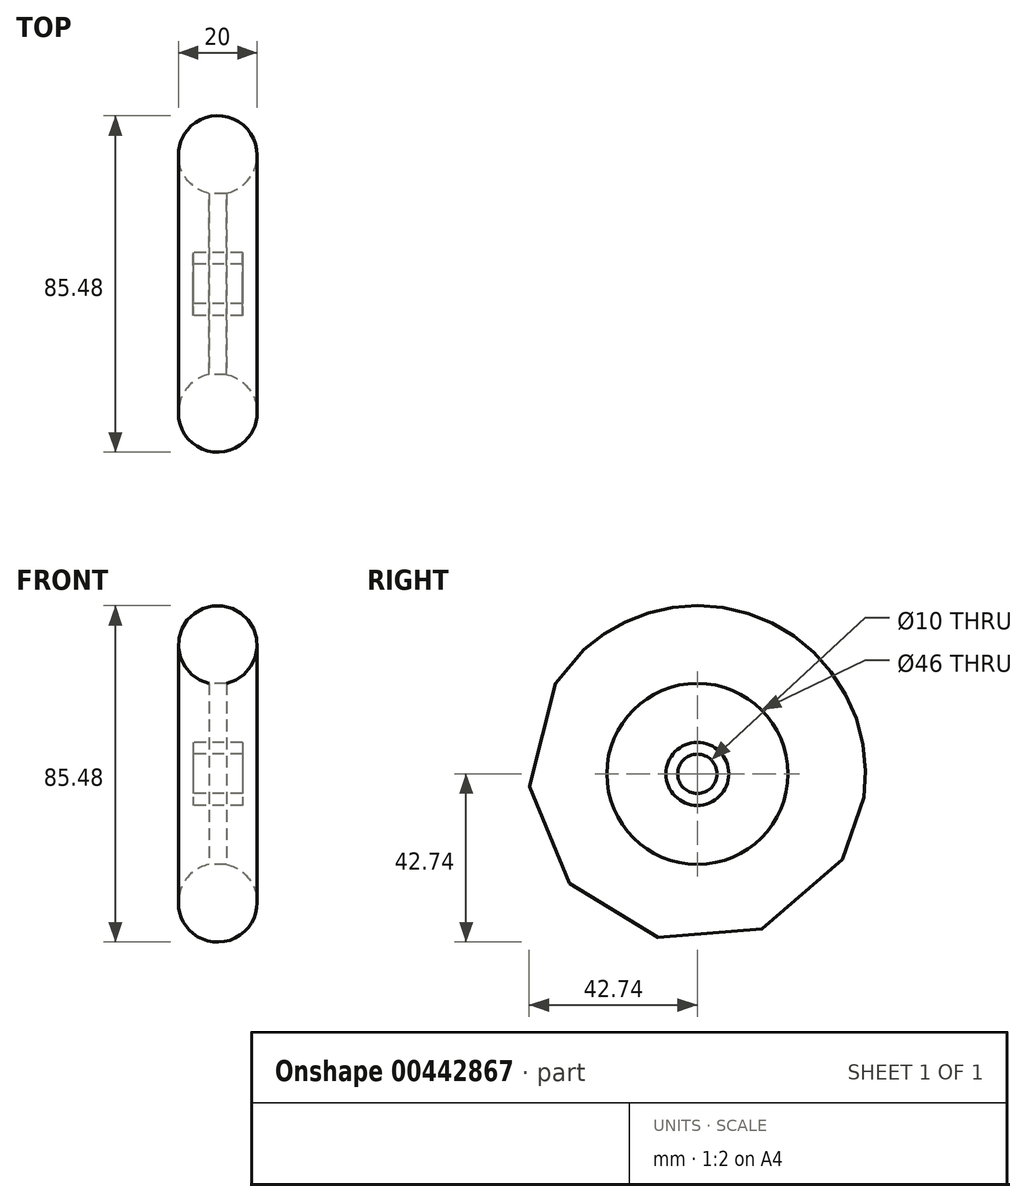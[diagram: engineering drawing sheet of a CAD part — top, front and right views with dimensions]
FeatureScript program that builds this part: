
annotation { "Feature Type Name" : "Feature", "Feature Type Description" : "" }
export const myFeature = defineFeature(function(context is Context, id is Id, definition is map)
    precondition{}
    {
        {
            var Q0;
            Q0=qCreatedBy(makeId("Front.planeOp"),FACE);
            var sketch = newSketch(context, id + "F0", { "sketchPlane" : qUnion([Q0])});
            skLineSegment(sketch, "E0.bottom", {"start": v(6.25, 8) * mm, "end": v(-6.25, 8) * mm});
            skLineSegment(sketch, "E0.top", {"start": v(6.25, 5) * mm, "end": v(-6.25, 5) * mm});
            skLineSegment(sketch, "E0.left", {"start": v(6.25, 8) * mm, "end": v(6.25, 5) * mm});
            skLineSegment(sketch, "E0.right", {"start": v(-6.25, 8) * mm, "end": v(-6.25, 5) * mm});
            skPoint(sketch, "E0.middle", {"position": v(0, 6.5) * mm});
            skLineSegment(sketch, "E1.bottom", {"start": v(-2.25, 8) * mm, "end": v(2.25, 8) * mm});
            skLineSegment(sketch, "E1.top", {"start": v(-2.25, 23) * mm, "end": v(2.25, 23) * mm});
            skLineSegment(sketch, "E1.left", {"start": v(-2.25, 8) * mm, "end": v(-2.25, 23) * mm});
            skLineSegment(sketch, "E1.right", {"start": v(2.25, 8) * mm, "end": v(2.25, 23) * mm});
            skArc(sketch, "E2", {"start": v(2.25, 23) * mm, "mid": v(0, 42.74) * mm, "end": v(-2.25, 23) * mm});
            skSolve(sketch);
        }
        {
            var Q0;
            Q0=qCreatedBy(makeId("Front.planeOp"),FACE);
            var sketch = newSketch(context, id + "F1", { "sketchPlane" : qUnion([Q0])});
            skLineSegment(sketch, "E3", {"start": v(-46.24, 0) * mm, "end": v(65.98, 0) * mm});
            skSolve(sketch);
        }
        {
            var Q0;
            Q0=makeQuery(id+"F0.imprint","IMPRINT",FACE,{"disambiguationData":[TD([[makeQuery(id+"F0.imprint","IMPRINT",EDGE,{"derivedFrom":sQuery(id+"F0.wireOp",EDGE,"E0.top")}),-1.0]])]});
            var Q1;
            Q1=makeQuery(id+"F0.imprint","IMPRINT",FACE,{"disambiguationData":[TD([[makeQuery(id+"F0.imprint","IMPRINT",EDGE,{"derivedFrom":sQuery(id+"F0.wireOp",EDGE,"E1.bottom")}),1.0]])]});
            var Q2;
            Q2=makeQuery(id+"F0.imprint","IMPRINT",FACE,{"disambiguationData":[TD([[makeQuery(id+"F0.imprint","IMPRINT",EDGE,{"derivedFrom":sQuery(id+"F0.wireOp",EDGE,"E1.top")}),1.0]])]});
            var Q3;
            Q3=sQuery(id+"F1.wireOp",EDGE,"E3");
            revolve(context, id + "F2", {"entities" : qUnion([Q0, Q1, Q2]), "axis" : qUnion([Q3]), "revolveType" : RevolveType.FULL});
        }
    });
